# Revit family: Deca_Cuba de apoio quadrada com mesa_Cubas Apoio_L.73
name_source: partatom
category: Plumbing Fixtures
units: mm (PartAtom-declared; Revit-internal decimal feet)

## family parameters
Cut with Voids When Loaded = Yes
Host = Face
Part Type = Normal
Room Calculation Point = No
Round Connector Dimension = Use Radius
Shared = No

## types (5) — shared parameters
Acompanha o Produto = -
Aprovado por = quattroD
Atendimento ao Cliente = 0800-0117073
Categoria = CUBAS
Composição Anel Vedação = -
Composição Assento = -
Composição Básica = Argila, feldspato, caulim, vidrados e corantes inorgânicos.
Composição Componente = Não Possui
Consumo = -
Cor Interna = -
Cor Secundária = -
Cores Componente = Não Possui
Criado por = quattroD
Código Pai = L.73
Description = Cuba de apoio quadrada com mesa
Diâmetro Ponto de Esgoto = 25 mm  [stored 0.082021 ft]
Informações Complementares = -
Itens de Instalação = 1601.C; 1601.C.CLI; 1602.C; 1602.C.PLA; 1680.C.100.112; 1682.C.100.112; 1684.C.100.112
Linha = Cubas Apoio
Manufacturer = Deca
Norma = NBR-16728-1;NBR-16728-2
Peso Líquido (Kg) = 14.558
Pressão máx. funcionamento = -
Pressão mín. Aquec. Acúmulo = -
Pressão mín. Aquec. Passagem = -
Pressão mín. funcionamento = -
Raio Ponto de Esgoto = 13 mm  [stored 0.0426509 ft]
Saída de Esgoto = Válvula Longa
Segmento = Banheiro Luxo
Tipo de dispositivo economizador = -
Tipo de mecanismo utilizado = -
Tipo de rosca de entrada = -
Tipo de rosca de saída = -
URL = www.deca.com.br
Vazão na Pressão máx. (L/min) = -
Vazão na Pressão mín. (L/min) = -
zero-valued in all types: Default Elevation

## per-type parameters (varying)
| type | Cor Principal | Material | Model |
| L.73.17_Branco | Branco | Deca_Branco | L.73.17 |
| L.73.37_Creme | Creme | Deca_Creme | L.73.37 |
| L.73.22_Marrom Fosco | Marrom Fosco | Deca_Marrom Fosco | L.73.22 |
| L.73.94_Ébano Fosco | Ébano Fosco | Deca_Ébano Fosco | L.73.94 |
| L.73.95_Ébano | Ébano | Deca_Ébano | L.73.95 |

note: [stored X ft] marks values corroborated as IEEE doubles in the binary element streams (Revit-internal decimal feet)

## geometry (parser evidence)
native form markers: Sweep x2
no freeform markers — native parametric forms only
